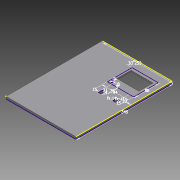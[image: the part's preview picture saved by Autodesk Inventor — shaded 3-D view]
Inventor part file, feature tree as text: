
AUTODESK INVENTOR PART (.ipt)
format: ipt  version: 2015 SP1 (Build 190203100, 203)  size: 450,560 bytes
history: native  units: mm
features: extrude x4, sketch x4
ambient origin geometry x8: Origin, YZ Plane, XZ Plane, XY Plane, X Axis, Y Axis, Z Axis, Center Point
bodies: Solid1 (feature_tree)
feature tree (8):
  extrude  "Extrusion1"  Depth=345.0mm
  sketch  "Sketch2"  dims[d2=8.0mm d3=0.0mm d4=94.0mm]
  extrude  "Extrusion2"  Depth=94.0mm
  extrude  "Extrusion3"  Depth=20.0mm
  extrude  "Extrusion4"  Depth=3.5mm
  sketch  "Sketch1"  dims[d0=250.0mm d1=345.0mm]
  sketch  "Sketch3"  dims[d5=88.0mm d6=20.0mm]
  sketch  "Sketch4"  dims[d7=30.0mm d8=9.0mm d9=9.0mm d10=8.0mm d11=11.0mm d12=14.0mm d13=11.0mm d14=14.0mm d15=15.0mm d16=15.0mm d17=35.0mm d18=4.0mm d19=0.0mm d20=94.0mm d21=30.0mm d22=88.0mm d23=20.0mm d24=3.5mm d25=0.0mm d26=8.0mm d27=7.0mm d28=10.0mm d29=27.0mm d30=3.5mm d31=0.0mm]
